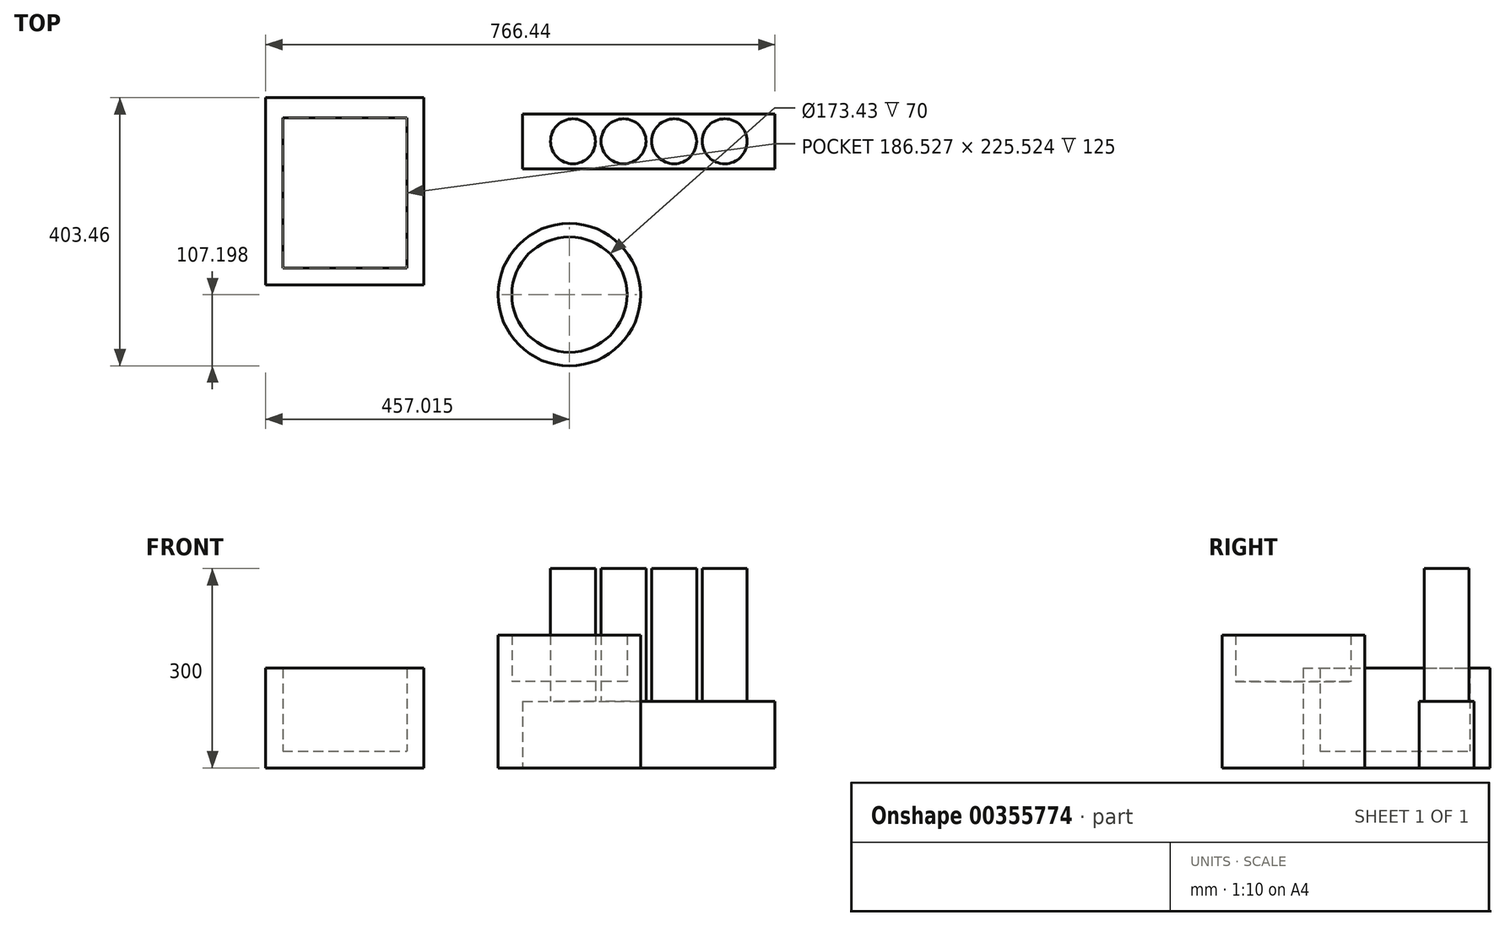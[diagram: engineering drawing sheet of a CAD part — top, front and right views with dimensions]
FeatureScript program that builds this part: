
annotation { "Feature Type Name" : "Feature", "Feature Type Description" : "" }
export const myFeature = defineFeature(function(context is Context, id is Id, definition is map)
    precondition{}
    {
        {
            var Q0;
            Q0=qCreatedBy(makeId("Top.planeOp"),FACE);
            var sketch = newSketch(context, id + "F0", { "sketchPlane" : qUnion([Q0])});
            skLineSegment(sketch, "E0.bottom", {"start": v(-438.9, 4284.66) * mm, "end": v(-201.06, 4284.66) * mm});
            skLineSegment(sketch, "E0.top", {"start": v(-438.9, 4566.3) * mm, "end": v(-201.06, 4566.3) * mm});
            skLineSegment(sketch, "E0.left", {"start": v(-438.9, 4284.66) * mm, "end": v(-438.9, 4566.3) * mm});
            skLineSegment(sketch, "E0.right", {"start": v(-201.06, 4284.66) * mm, "end": v(-201.06, 4566.3) * mm});
            skLineSegment(sketch, "E1.bottom", {"start": v(-52.2, 4459.58) * mm, "end": v(327.53, 4459.58) * mm});
            skLineSegment(sketch, "E1.top", {"start": v(-52.2, 4542.06) * mm, "end": v(327.53, 4542.06) * mm});
            skLineSegment(sketch, "E1.left", {"start": v(-52.2, 4459.58) * mm, "end": v(-52.2, 4542.06) * mm});
            skLineSegment(sketch, "E1.right", {"start": v(327.53, 4459.58) * mm, "end": v(327.53, 4542.06) * mm});
            skCircle(sketch, "E2", {"center": v(251.85, 4500.82) * mm, "radius": 33.8 * mm});
            skPoint(sketch, "E2.centerSnap0", {"position": v(-52.2, 4500.82) * mm});
            skCircle(sketch, "E3", {"center": v(175.73, 4500.82) * mm, "radius": 33.8 * mm});
            skPoint(sketch, "E3.centerSnap0", {"position": v(327.53, 4500.82) * mm});
            skCircle(sketch, "E4", {"center": v(99.6, 4500.82) * mm, "radius": 33.8 * mm});
            skCircle(sketch, "E5", {"center": v(23.48, 4500.82) * mm, "radius": 33.8 * mm});
            skLineSegment(sketch, "E6.bottom", {"start": v(-413.25, 4310.32) * mm, "end": v(-226.72, 4310.32) * mm});
            skLineSegment(sketch, "E6.top", {"start": v(-413.25, 4535.84) * mm, "end": v(-226.72, 4535.84) * mm});
            skLineSegment(sketch, "E6.left", {"start": v(-413.25, 4310.32) * mm, "end": v(-413.25, 4535.84) * mm});
            skLineSegment(sketch, "E6.right", {"start": v(-226.72, 4310.32) * mm, "end": v(-226.72, 4535.84) * mm});
            skCircle(sketch, "E7", {"center": v(18.1, 4270.05) * mm, "radius": 107.2 * mm});
            skCircle(sketch, "E8", {"center": v(18.1, 4270.05) * mm, "radius": 86.72 * mm});
            skLineSegment(sketch, "E9", {"start": v(327.53, 4500.82) * mm, "end": v(251.85, 4500.82) * mm, "construction": true});
            skLineSegment(sketch, "E10", {"start": v(-52.2, 4500.82) * mm, "end": v(23.48, 4500.82) * mm, "construction": true});
            skLineSegment(sketch, "E11", {"start": v(251.85, 4500.82) * mm, "end": v(175.73, 4500.82) * mm, "construction": true});
            skLineSegment(sketch, "E12", {"start": v(175.73, 4500.82) * mm, "end": v(99.6, 4500.82) * mm, "construction": true});
            skLineSegment(sketch, "E13", {"start": v(99.6, 4500.82) * mm, "end": v(23.48, 4500.82) * mm, "construction": true});
            skLineSegment(sketch, "E14", {"start": v(-264.08, 4310.32) * mm, "end": v(-264.08, 4284.66) * mm, "construction": true});
            skLineSegment(sketch, "E15", {"start": v(-265.9, 4561.5) * mm, "end": v(-265.9, 4535.84) * mm, "construction": true});
            skLineSegment(sketch, "E16", {"start": v(-201.06, 4475.28) * mm, "end": v(-226.72, 4475.28) * mm, "construction": true});
            skLineSegment(sketch, "E17", {"start": v(-413.25, 4463.82) * mm, "end": v(-438.9, 4463.82) * mm, "construction": true});
            skLineSegment(sketch, "E18", {"start": v(-39.8, 4334.6) * mm, "end": v(-39.8, 4360.25) * mm, "construction": true});
            skSolve(sketch);
        }
        {
            var Q0;
            Q0=makeQuery(id+"F0.imprint","IMPRINT",FACE,{"disambiguationData":[TD([[makeQuery(id+"F0.imprint","IMPRINT",EDGE,{"derivedFrom":sQuery(id+"F0.wireOp",EDGE,"E1.bottom")}),1.0]])]});
            extrude(context, id + "F1", {"entities" : qUnion([Q0]), "depth" : 100 * mm});
        }
        {
            var Q0;
            Q0=makeQuery(id+"F0.imprint","IMPRINT",FACE,{"disambiguationData":[TD([[makeQuery(id+"F0.imprint","IMPRINT",EDGE,{"derivedFrom":sQuery(id+"F0.wireOp",EDGE,"E2")}),1.0]])]});
            var Q1;
            Q1=makeQuery(id+"F0.imprint","IMPRINT",FACE,{"disambiguationData":[TD([[makeQuery(id+"F0.imprint","IMPRINT",EDGE,{"derivedFrom":sQuery(id+"F0.wireOp",EDGE,"E3")}),1.0]])]});
            var Q2;
            Q2=makeQuery(id+"F0.imprint","IMPRINT",FACE,{"disambiguationData":[TD([[makeQuery(id+"F0.imprint","IMPRINT",EDGE,{"derivedFrom":sQuery(id+"F0.wireOp",EDGE,"E4")}),1.0]])]});
            var Q3;
            Q3=makeQuery(id+"F0.imprint","IMPRINT",FACE,{"disambiguationData":[TD([[makeQuery(id+"F0.imprint","IMPRINT",EDGE,{"derivedFrom":sQuery(id+"F0.wireOp",EDGE,"E5")}),1.0]])]});
            extrude(context, id + "F2", {"entities" : qUnion([Q0, Q1, Q2, Q3]), "operationType" : NewBodyOperationType.ADD, "depth" : 300 * mm});
        }
        {
            var Q0;
            {var subQ2=sQuery(id+"F0.wireOp",EDGE,"E0.top");Q0=makeQuery(id+"F0.imprint","IMPRINT",FACE,{"disambiguationData":[TD([[makeQuery(id+"F0.imprint","IMPRINT",EDGE,{"derivedFrom":subQ2}),-1.0]])]});}
            var Q1;
            {var subQ2=sQuery(id+"F0.wireOp",EDGE,"E0.bottom");Q1=makeQuery(id+"F0.imprint","IMPRINT",FACE,{"disambiguationData":[TD([[makeQuery(id+"F0.imprint","IMPRINT",EDGE,{"derivedFrom":subQ2}),1.0]])]});}
            extrude(context, id + "F3", {"entities" : qUnion([Q0, Q1]), "depth" : 150 * mm});
        }
        {
            var Q0;
            {var subQ0=sQuery(id+"F0.wireOp",EDGE,"E6.bottom");Q0=makeQuery(id+"F0.imprint","IMPRINT",FACE,{"disambiguationData":[TD([[makeQuery(id+"F0.imprint","IMPRINT",EDGE,{"derivedFrom":subQ0}),1.0]])]});}
            var Q1;
            {var subQ0=sQuery(id+"F0.wireOp",EDGE,"E6.top");Q1=makeQuery(id+"F0.imprint","IMPRINT",FACE,{"disambiguationData":[TD([[makeQuery(id+"F0.imprint","IMPRINT",EDGE,{"derivedFrom":subQ0}),-1.0]])]});}
            extrude(context, id + "F4", {"entities" : qUnion([Q0, Q1]), "operationType" : NewBodyOperationType.ADD, "depth" : 25 * mm});
        }
        {
            var Q0;
            Q0=makeQuery(id+"F0.imprint","IMPRINT",FACE,{"disambiguationData":[TD([[makeQuery(id+"F0.imprint","IMPRINT",EDGE,{"derivedFrom":sQuery(id+"F0.wireOp",EDGE,"E7")}),1.0]])]});
            extrude(context, id + "F5", {"entities" : qUnion([Q0]), "depth" : 200 * mm});
        }
        {
            var Q0;
            Q0=makeQuery(id+"F0.imprint","IMPRINT",FACE,{"disambiguationData":[TD([[makeQuery(id+"F0.imprint","IMPRINT",EDGE,{"derivedFrom":sQuery(id+"F0.wireOp",EDGE,"E8")}),1.0]])]});
            extrude(context, id + "F6", {"entities" : qUnion([Q0]), "operationType" : NewBodyOperationType.ADD, "depth" : 130 * mm});
        }
    });
